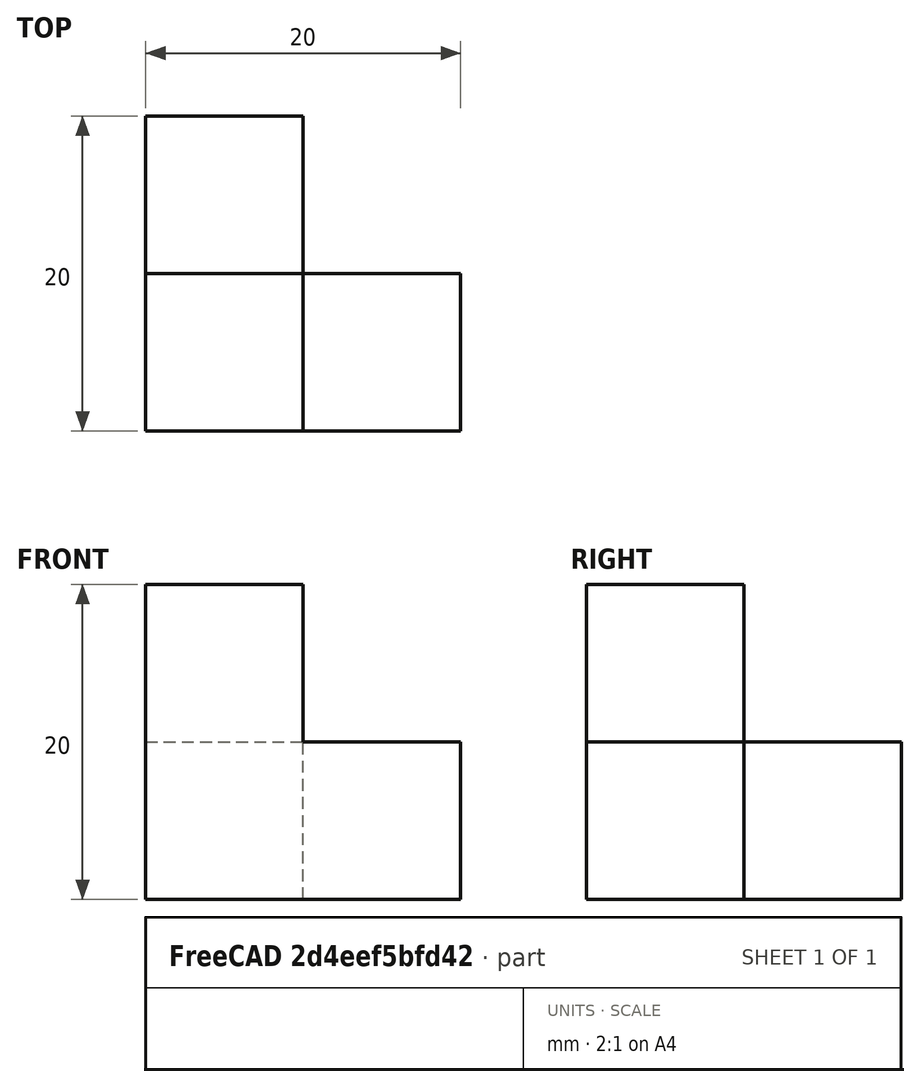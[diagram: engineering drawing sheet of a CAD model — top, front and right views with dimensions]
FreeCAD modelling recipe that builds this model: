
FCSTD DOCUMENT  (FreeCAD 1.0R39319 (Git))
Label: ojt1_t05r01_refine shape
License: All rights reserved
LicenseURL: https://en.wikipedia.org/wiki/All_rights_reserved
objects: Part::Box×4, Part::MultiFuse×1
note: 5 computed .brp shape members not serialized (recipe doc carries the construction recipe); baked Part::Feature solids carry a one-line shape summary decoded from their .brp

FEATURE [Part::Box] Box  label="Cub"
  AttacherType = Attacher::AttachEngine3D
  Height = 10
  Length = 10
  Width = 10
FEATURE [Part::Box] Box001  label="Cub001"
  AttacherType = Attacher::AttachEngine3D
  Height = 10
  Length = 10
  Placement = pos=(10,0,0) rot=(0,0,1;0rad)
  Width = 10
FEATURE [Part::Box] Box002  label="Cub002"
  AttacherType = Attacher::AttachEngine3D
  Height = 10
  Length = 10
  Placement = pos=(0,10,0) rot=(0,0,1;0rad)
  Width = 10
FEATURE [Part::Box] Box003  label="Cub003"
  AttacherType = Attacher::AttachEngine3D
  Height = 10
  Length = 10
  Placement = pos=(0,0,10) rot=(0,0,1;0rad)
  Width = 10
FEATURE [Part::MultiFuse] Fusion
  Refine = true
  Shapes = -> [Box,Box001,Box002,Box003]
